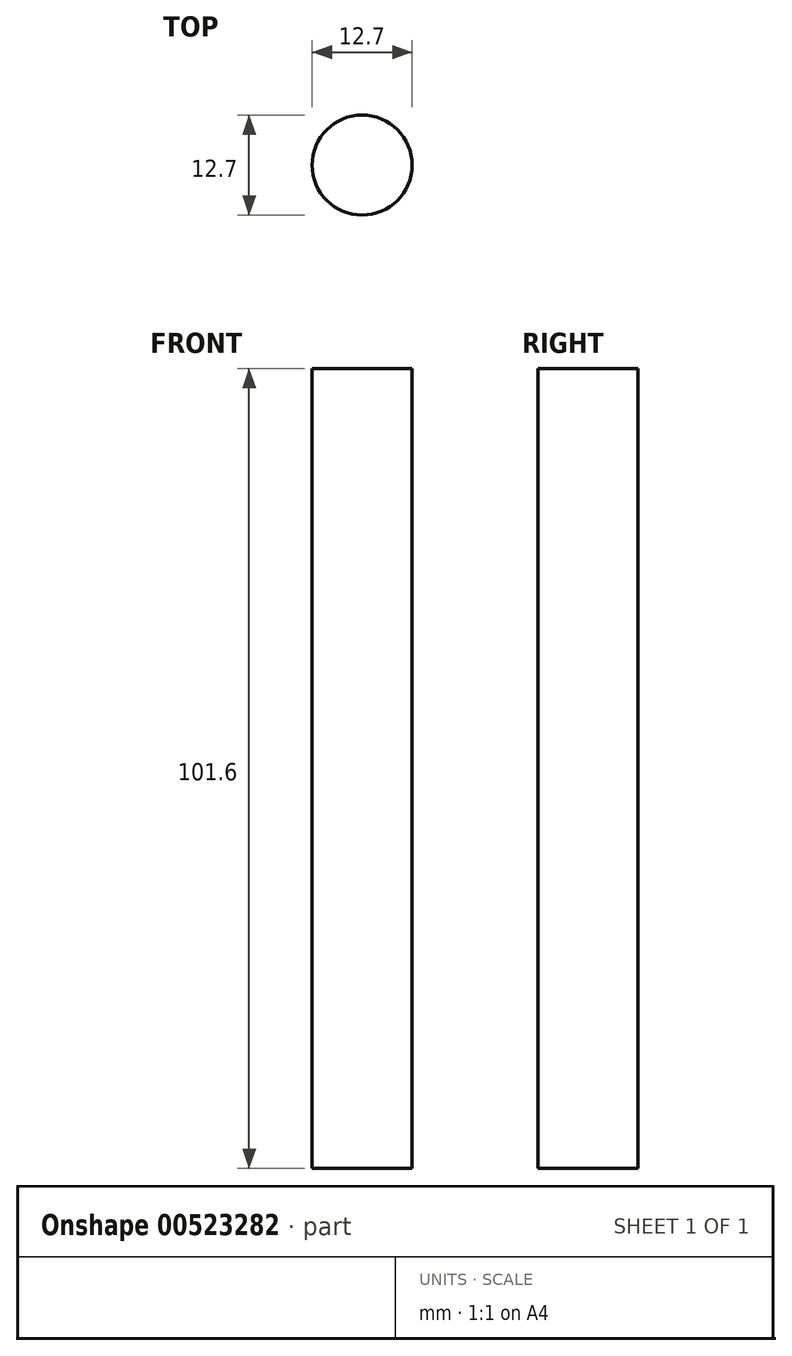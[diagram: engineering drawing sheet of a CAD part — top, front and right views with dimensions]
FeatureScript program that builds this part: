
annotation { "Feature Type Name" : "Feature", "Feature Type Description" : "" }
export const myFeature = defineFeature(function(context is Context, id is Id, definition is map)
    precondition{}
    {
        {
            var Q0;
            Q0=qCreatedBy(makeId("Top.planeOp"),FACE);
            var sketch = newSketch(context, id + "F0", { "sketchPlane" : qUnion([Q0])});
            skCircle(sketch, "E0", {"center": v(0, 0) * mm, "radius": 6.35 * mm});
            skSolve(sketch);
        }
        {
            var Q0;
            Q0=makeQuery(id+"F0.imprint","IMPRINT",FACE,{"disambiguationData":[TD([[makeQuery(id+"F0.imprint","IMPRINT",EDGE,{"derivedFrom":sQuery(id+"F0.wireOp",EDGE,"E0")}),1.0]])]});
            extrude(context, id + "F1", {"entities" : qUnion([Q0]), "depth" : 101.6 * mm, "offsetDistance" : 25.4 * mm});
        }
    });
